# Revit family: Hager-Volta-IP30-Hollow_wall-leer-DE-de
name_source: partatom
category: Electrical Equipment
units: mm (PartAtom-declared; Revit-internal decimal feet)

## family parameters
Cut with Voids When Loaded = No
Host = Face
Panel Configuration = Two Columns, Circuits Across
Part Type = Panelboard
Room Calculation Point = No
Round Connector Dimension = Use Diameter
Shared = No

## types (22) — shared parameters
EF000003 - Montageart = EV000128 - Hohlwand
EF000007 - Farbe = EV000202 - weiß
EF000116 - RAL-Nummer = 9010
EF000846 - Einbaubreite = 314 mm  [stored 1.03018 ft]
EF001088 - Anbaumöglichkeit = Yes
EF001131 - Innentiefe = 92 mm  [stored 0.301837 ft]
EF002950 - Breite in Teilungseinheiten = 12
EF006244 - Transparenter Deckel/Tür = No
EF006306 - Mit Schloss = No
EF015776 - Erdungsklemmenblock = No
EF015777 - Neutralleiterklemmenblock = No
HG000003 - Bereich = Volta
HG000005 - Dicke = 3 mm  [stored 0.00984252 ft]
HG000006 - Unterputz = Yes
HG000009 - Doppelflügeligen Tür = No
HG000010 - Asymmetrische Türen = No
HG000011 - Leere Reihen von unten = No
HG000017 - Distanz zwischen den Polen = 18 mm  [stored 0.0590551 ft]
Manufacturer = Hager
Type Comments = Volta
zero-valued in all types: Default Elevation, HG000001 - Anzahl der Spalten, HG000007 - Anzahl der leeren Spalten, HG000008 - Anzahl der leeren Reihen

## per-type parameters (varying)
| type | EF000008 - Breite | EF000040 - Höhe | EF000049 - Tiefe | EF000118 - Mit Montageplatte | EF000218 - Einbautiefe | EF000266 - Anzahl der Reihen | EF000332 - Einbauhöhe | EF000339 - Art der Abdeckung | EF001062 - EMV-Ausführung | EF001134 - DIN-Schiene | EF001596 - Werkstoff des Gehäuses | EF004462 - Art der Schließung | EF005474 - Schutzart (IP) | EF009212 - Ausführung Deckel | EF015941 - Signaldurchlassende Tür | HG000002 - Mit tür | HG000004 - Herstellerreferenz | Model |
| Unterputz  B330 H355 T94.5 12 Teilungseinheiten - VH12NK | 330 mm | 355 mm | 94 mm  [stored 0.308399 ft] | No | 90 mm  [stored 0.295276 ft] | 1 | 346 mm  [stored 1.13517 ft] |  | Yes | No | EV000139 - Kunststoff |  |  | EV000116 - geschlossen | No | No | VH12NK | VH12NK |
| Unterputz  B330 H484 T94.5 12 Teilungseinheiten - VH24NK | 330 mm | 484 mm  [stored 1.58793 ft] | 94 mm  [stored 0.308399 ft] | No | 90 mm  [stored 0.295276 ft] | 2 | 471 mm  [stored 1.54528 ft] |  | Yes | No | EV000139 - Kunststoff |  |  | EV000116 - geschlossen | No | No | VH24NK | VH24NK |
| Unterputz  B330 H609 T94.5 12 Teilungseinheiten - VH36NK | 330 mm | 609 mm  [stored 1.99803 ft] | 94 mm  [stored 0.308399 ft] | No | 90 mm  [stored 0.295276 ft] | 3 | 596 mm  [stored 1.95538 ft] |  | Yes | No | EV000139 - Kunststoff |  |  | EV000116 - geschlossen | No | No | VH36NK | VH36NK |
| Unterputz  B330 H734 T94.5 12 Teilungseinheiten - VH48NK | 330 mm | 734 mm  [stored 2.40814 ft] | 94 mm  [stored 0.308399 ft] | No | 90 mm  [stored 0.295276 ft] | 4 | 721 mm  [stored 2.36549 ft] |  | Yes | No | EV000139 - Kunststoff |  |  | EV000116 - geschlossen | No | No | VH48NK | VH48NK |
| Unterputz  B330 H880 T94.5 12 Teilungseinheiten - VH60NK | 330 mm | 880 mm  [stored 2.88714 ft] | 94 mm  [stored 0.308399 ft] | No | 90 mm  [stored 0.295276 ft] | 5 | 846 mm  [stored 2.77559 ft] |  | Yes | No | EV000139 - Kunststoff |  |  | EV000116 - geschlossen | No | No | VH60NK | VH60NK |
| Unterputz  B348 H880 T94.5 12 Teilungseinheiten - VH60NKM | 348 mm  [stored 1.14173 ft] | 880 mm  [stored 2.88714 ft] | 94 mm  [stored 0.308399 ft] | Yes | 90 mm  [stored 0.295276 ft] | 5 | 846 mm  [stored 2.77559 ft] |  | No | Yes | EV000139 - Kunststoff |  |  | EV000116 - geschlossen | No | No | VH60NKM | VH60NKM |
| Unterputz IP30 B348 H505.5 T98 12 Teilungseinheiten - VH24NWB | 348 mm  [stored 1.14173 ft] | 506 mm  [stored 1.6601 ft] | 98 mm  [stored 0.321522 ft] | Yes | 89 mm  [stored 0.291995 ft] | 0 | 470 mm  [stored 1.54199 ft] | EV004216 - Tür | No | Yes | EV000154 - sonstige | EV000154 - sonstige | EV006410 - IP30 | EV009916 - mit Ausschnitt | No | Yes | VH24NWB | VH24NWB |
| Unterputz IP30 B348 H630.5 T98 12 Teilungseinheiten - VH36NKM | 348 mm  [stored 1.14173 ft] | 630 mm  [stored 2.06693 ft] | 98 mm  [stored 0.321522 ft] | Yes | 89 mm  [stored 0.291995 ft] | 0 | 595 mm  [stored 1.9521 ft] |  | No | Yes | EV000139 - Kunststoff |  | EV006410 - IP30 | EV000116 - geschlossen | No | No | VH36NKM | VH36NKM |
| Unterputz IP30 B348 H630.5 T98 12 Teilungseinheiten - VH36NW | 348 mm  [stored 1.14173 ft] | 630 mm  [stored 2.06693 ft] | 98 mm  [stored 0.321522 ft] | Yes | 89 mm  [stored 0.291995 ft] | 0 | 595 mm  [stored 1.9521 ft] | EV004216 - Tür | No | Yes | EV000154 - sonstige | EV000154 - sonstige | EV006410 - IP30 | EV009916 - mit Ausschnitt | No | Yes | VH36NW | VH36NW |
| Unterputz IP30 B348 H630.5 T98 12 Teilungseinheiten - VH36NWB | 348 mm  [stored 1.14173 ft] | 630 mm  [stored 2.06693 ft] | 98 mm  [stored 0.321522 ft] | Yes | 89 mm  [stored 0.291995 ft] | 0 | 595 mm  [stored 1.9521 ft] | EV004216 - Tür | No | Yes | EV000154 - sonstige | EV000154 - sonstige | EV006410 - IP30 | EV009916 - mit Ausschnitt | No | Yes | VH36NWB | VH36NWB |
| Unterputz IP30 B348 H630.5 T98 12 Teilungseinheiten - VH36WWH | 348 mm  [stored 1.14173 ft] | 630 mm  [stored 2.06693 ft] | 98 mm  [stored 0.321522 ft] | Yes | 89 mm  [stored 0.291995 ft] | 0 | 595 mm  [stored 1.9521 ft] | EV004216 - Tür | No | Yes | EV000154 - sonstige | EV000154 - sonstige | EV006410 - IP30 | EV009916 - mit Ausschnitt | Yes | Yes | VH36WWH | VH36WWH |
| Unterputz IP30 B348 H755.5 T98 12 Teilungseinheiten - VH48MMV | 348 mm  [stored 1.14173 ft] | 756 mm  [stored 2.48031 ft] | 98 mm  [stored 0.321522 ft] | Yes | 89 mm  [stored 0.291995 ft] | 0 | 720 mm  [stored 2.3622 ft] | EV004216 - Tür | No | Yes | EV000154 - sonstige | EV000154 - sonstige | EV006410 - IP30 | EV009916 - mit Ausschnitt | No | Yes | VH48MMV | VH48MMV |
| Unterputz IP30 B348 H755.5 T98 12 Teilungseinheiten - VH48NKM | 348 mm  [stored 1.14173 ft] | 756 mm  [stored 2.48031 ft] | 98 mm  [stored 0.321522 ft] | Yes | 89 mm  [stored 0.291995 ft] | 0 | 720 mm  [stored 2.3622 ft] |  | No | Yes | EV000139 - Kunststoff |  | EV006410 - IP30 | EV000116 - geschlossen | No | No | VH48NKM | VH48NKM |
| Unterputz IP30 B348 H755.5 T98 12 Teilungseinheiten - VH48NW | 348 mm  [stored 1.14173 ft] | 756 mm  [stored 2.48031 ft] | 98 mm  [stored 0.321522 ft] | Yes | 89 mm  [stored 0.291995 ft] | 0 | 720 mm  [stored 2.3622 ft] | EV004216 - Tür | No | Yes | EV000154 - sonstige | EV000154 - sonstige | EV006410 - IP30 | EV009916 - mit Ausschnitt | No | Yes | VH48NW | VH48NW |
| Unterputz IP30 B348 H755.5 T98 12 Teilungseinheiten - VH48NWB | 348 mm  [stored 1.14173 ft] | 756 mm  [stored 2.48031 ft] | 98 mm  [stored 0.321522 ft] | Yes | 89 mm  [stored 0.291995 ft] | 0 | 720 mm  [stored 2.3622 ft] | EV004216 - Tür | No | Yes | EV000154 - sonstige | EV000154 - sonstige | EV006410 - IP30 | EV009916 - mit Ausschnitt | No | Yes | VH48NWB | VH48NWB |
| Unterputz IP30 B348 H755.5 T98 12 Teilungseinheiten - VH48WWH | 348 mm  [stored 1.14173 ft] | 756 mm  [stored 2.48031 ft] | 98 mm  [stored 0.321522 ft] | Yes | 89 mm  [stored 0.291995 ft] | 0 | 720 mm  [stored 2.3622 ft] | EV004216 - Tür | No | Yes | EV000154 - sonstige | EV000154 - sonstige | EV006410 - IP30 | EV009916 - mit Ausschnitt | Yes | Yes | VH48WWH | VH48WWH |
| Unterputz IP30 B348 H755.5 T98 12 Teilungseinheiten - VH48WWV | 348 mm  [stored 1.14173 ft] | 756 mm  [stored 2.48031 ft] | 98 mm  [stored 0.321522 ft] | Yes | 89 mm  [stored 0.291995 ft] | 0 | 720 mm  [stored 2.3622 ft] | EV004216 - Tür | No | Yes | EV000154 - sonstige | EV000154 - sonstige | EV006410 - IP30 | EV009916 - mit Ausschnitt | Yes | Yes | VH48WWV | VH48WWV |
| Unterputz IP30 B348 H880.5 T98 12 Teilungseinheiten - VH60MMV | 348 mm  [stored 1.14173 ft] | 880 mm  [stored 2.88714 ft] | 98 mm  [stored 0.321522 ft] | Yes | 89 mm  [stored 0.291995 ft] | 0 | 845 mm  [stored 2.77231 ft] | EV004216 - Tür | No | Yes | EV000154 - sonstige | EV000154 - sonstige | EV006410 - IP30 | EV009916 - mit Ausschnitt | No | Yes | VH60MMV | VH60MMV |
| Unterputz IP30 B348 H880.5 T98 12 Teilungseinheiten - VH60NW | 348 mm  [stored 1.14173 ft] | 880 mm  [stored 2.88714 ft] | 98 mm  [stored 0.321522 ft] | Yes | 89 mm  [stored 0.291995 ft] | 0 | 845 mm  [stored 2.77231 ft] | EV004216 - Tür | No | Yes | EV000154 - sonstige | EV000154 - sonstige | EV006410 - IP30 | EV009916 - mit Ausschnitt | No | Yes | VH60NW | VH60NW |
| Unterputz IP30 B348 H880.5 T98 12 Teilungseinheiten - VH60NWB | 348 mm  [stored 1.14173 ft] | 880 mm  [stored 2.88714 ft] | 98 mm  [stored 0.321522 ft] | Yes | 89 mm  [stored 0.291995 ft] | 0 | 845 mm  [stored 2.77231 ft] | EV004216 - Tür | No | Yes | EV000154 - sonstige | EV000154 - sonstige | EV006410 - IP30 | EV009916 - mit Ausschnitt | No | Yes | VH60NWB | VH60NWB |
| Unterputz IP30 B348 H880.5 T98 12 Teilungseinheiten - VH60WWH | 348 mm  [stored 1.14173 ft] | 880 mm  [stored 2.88714 ft] | 98 mm  [stored 0.321522 ft] | Yes | 89 mm  [stored 0.291995 ft] | 0 | 845 mm  [stored 2.77231 ft] | EV004216 - Tür | No | Yes | EV000154 - sonstige | EV000154 - sonstige | EV006410 - IP30 | EV009916 - mit Ausschnitt | Yes | Yes | VH60WWH | VH60WWH |
| Unterputz IP30 B348 H880.5 T98 12 Teilungseinheiten - VH60WWV | 348 mm  [stored 1.14173 ft] | 880 mm  [stored 2.88714 ft] | 98 mm  [stored 0.321522 ft] | Yes | 89 mm  [stored 0.291995 ft] | 0 | 845 mm  [stored 2.77231 ft] | EV004216 - Tür | No | Yes | EV000154 - sonstige | EV000154 - sonstige | EV006410 - IP30 | EV009916 - mit Ausschnitt | Yes | Yes | VH60WWV | VH60WWV |

note: [stored X ft] marks values corroborated as IEEE doubles in the binary element streams (Revit-internal decimal feet)

## geometry (parser evidence)
native form markers: Sweep x17
no freeform markers — native parametric forms only
